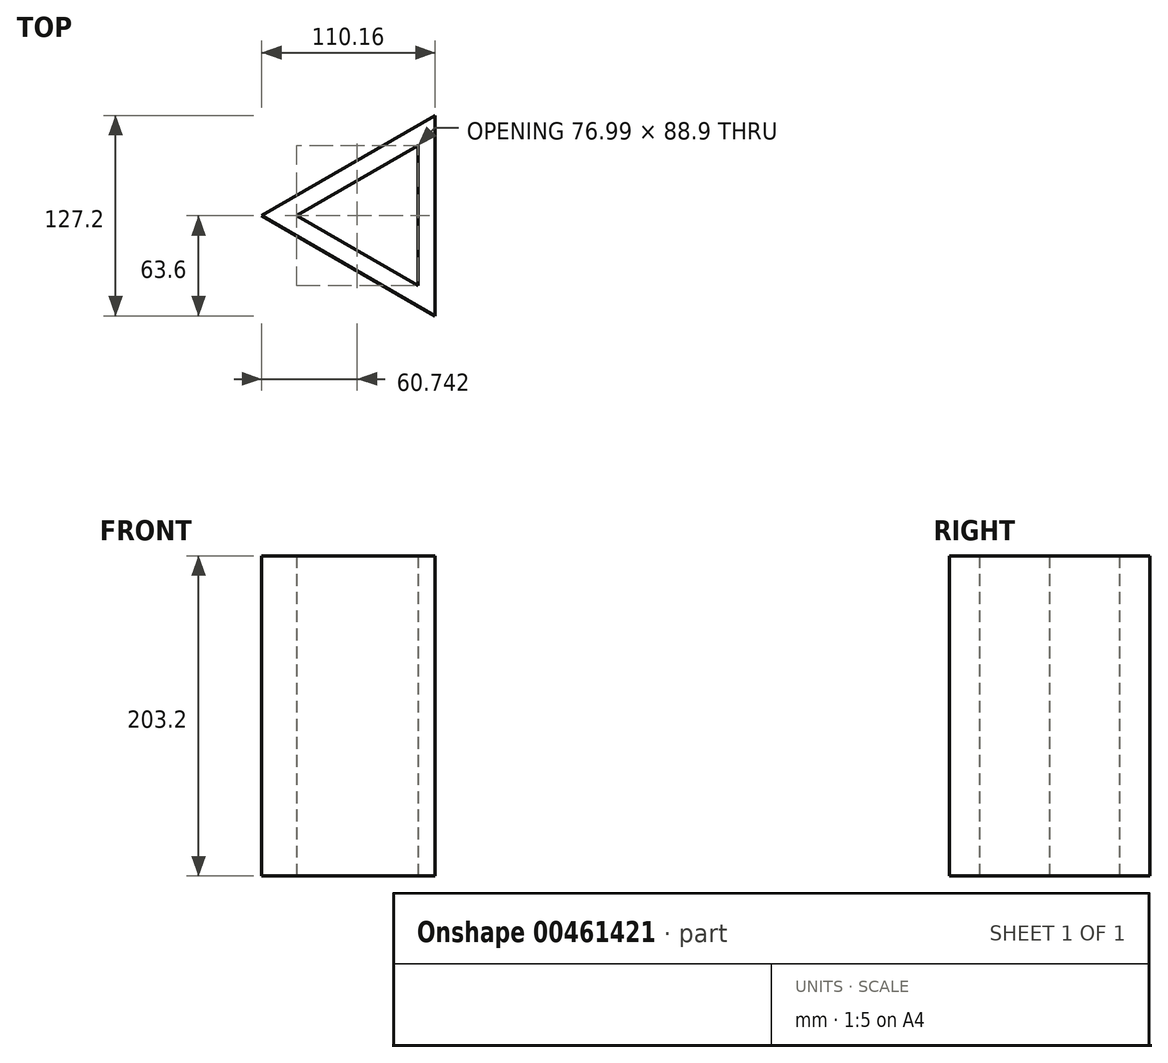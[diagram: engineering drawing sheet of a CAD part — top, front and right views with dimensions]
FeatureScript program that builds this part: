
annotation { "Feature Type Name" : "Feature", "Feature Type Description" : "" }
export const myFeature = defineFeature(function(context is Context, id is Id, definition is map)
    precondition{}
    {
        {
            var Q0;
            Q0=qCreatedBy(makeId("Top.planeOp"),FACE);
            var sketch = newSketch(context, id + "F0", { "sketchPlane" : qUnion([Q0])});
            skLineSegment(sketch, "E0", {"start": v(-48.88, 0) * mm, "end": v(28.1, -44.45) * mm});
            skLineSegment(sketch, "E1", {"start": v(28.1, -44.45) * mm, "end": v(28.1, 44.45) * mm});
            skLineSegment(sketch, "E2", {"start": v(28.1, 44.45) * mm, "end": v(-48.88, 0) * mm});
            skLineSegment(sketch, "E3", {"start": v(-71.13, 0) * mm, "end": v(39.03, -63.6) * mm});
            skLineSegment(sketch, "E4", {"start": v(39.03, -63.6) * mm, "end": v(39.03, 63.6) * mm});
            skLineSegment(sketch, "E5", {"start": v(39.03, 63.6) * mm, "end": v(-71.13, 0) * mm});
            skSolve(sketch);
        }
        {
            var Q0;
            Q0 = qSketchRegion(id + "F0", true);
            extrude(context, id + "F1", {"entities" : qUnion([Q0]), "endBound" : BoundingType.SYMMETRIC, "depth" : 203.2 * mm});
        }
    });
